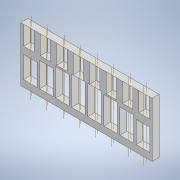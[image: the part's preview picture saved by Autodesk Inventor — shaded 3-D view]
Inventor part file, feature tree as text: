
AUTODESK INVENTOR PART (.ipt)
format: ipt  version: 2022 (Build 260153000, 153)  size: 300,032 bytes
history: native  units: mm
features: other x16, projected_geometry x16, sketch x5, extrude x3, pattern_linear x1, plane x1, mirror x1, chamfer x1
ambient origin geometry x8: Origin, YZ Plane, XZ Plane, XY Plane, X Axis, Y Axis, Z Axis, Center Point
bodies: Solid1 (feature_tree)
feature tree (44):
  extrude  "Extrusion1"  Depth=100.0mm
  extrude  "Extrusion2"  Depth=19.0mm
  pattern_linear  "Rectangular Pattern2"  Count1=3  [1 undecoded]
  extrude  "Extrusion3"  Depth=5.0mm
  plane  "Work Plane1"
  mirror  "Mirror1"
  sketch  "Sketch4"  dims[d30=80.0mm d32=211.0mm]
  other  "Work Axis1"
  other  "Work Axis2"
  other  "Work Axis3"
  other  "Work Axis4"
  other  "Work Axis5"
  other  "Work Axis6"
  other  "Work Axis15"
  other  "Work Axis16"
  sketch  "Sketch5"  dims[d33=25.0mm d34=48.0mm d37=35.0mm d38=40.0mm d39=45.0mm d40=5.0mm d41=2.222222mm d42=4.444444mm d43=4.444444mm d44=4.444444mm d45=4.444444mm d46=12.7mm d47=0.0mm d48=8.5mm d49=11.5mm d50=5.0mm d51=2.0mm d52=45.0deg]
  other  "Work Axis7"
  other  "Work Axis8"
  other  "Work Axis9"
  other  "Work Axis10"
  other  "Work Axis11"
  other  "Work Axis12"
  other  "Work Axis13"
  other  "Work Axis14"
  chamfer  "Chamfer1"  Distance=12.7mm
  sketch  "Sketch1"  dims[d0=240.0mm d1=100.0mm]
  sketch  "Sketch2"  dims[d2=12.7mm d3=0.0mm d24=19.0mm d25=30.0mm]
  sketch  "Sketch3"  dims[d26=5.0mm d27=5.0mm d28=12.7mm d29=0.0mm]
  projected_geometry  "Projected Loop1"
  projected_geometry  "Projected Loop2"
  projected_geometry  "Projected Loop3"
  projected_geometry  "Projected Loop4"
  projected_geometry  "Projected Loop5"
  projected_geometry  "Projected Loop6"
  projected_geometry  "Projected Loop7"
  projected_geometry  "Projected Loop8"
  projected_geometry  "Projected Loop9"
  projected_geometry  "Projected Loop10"
  projected_geometry  "Projected Loop11"
  projected_geometry  "Projected Loop12"
  projected_geometry  "Projected Loop13"
  projected_geometry  "Projected Loop14"
  projected_geometry  "Projected Loop15"
  projected_geometry  "Projected Loop16"
note: 1 required parameter value undecoded (feature->parameter linkage not recoverable at this tier; creation-order binding heuristic only, values carry confidence <= 0.55)
